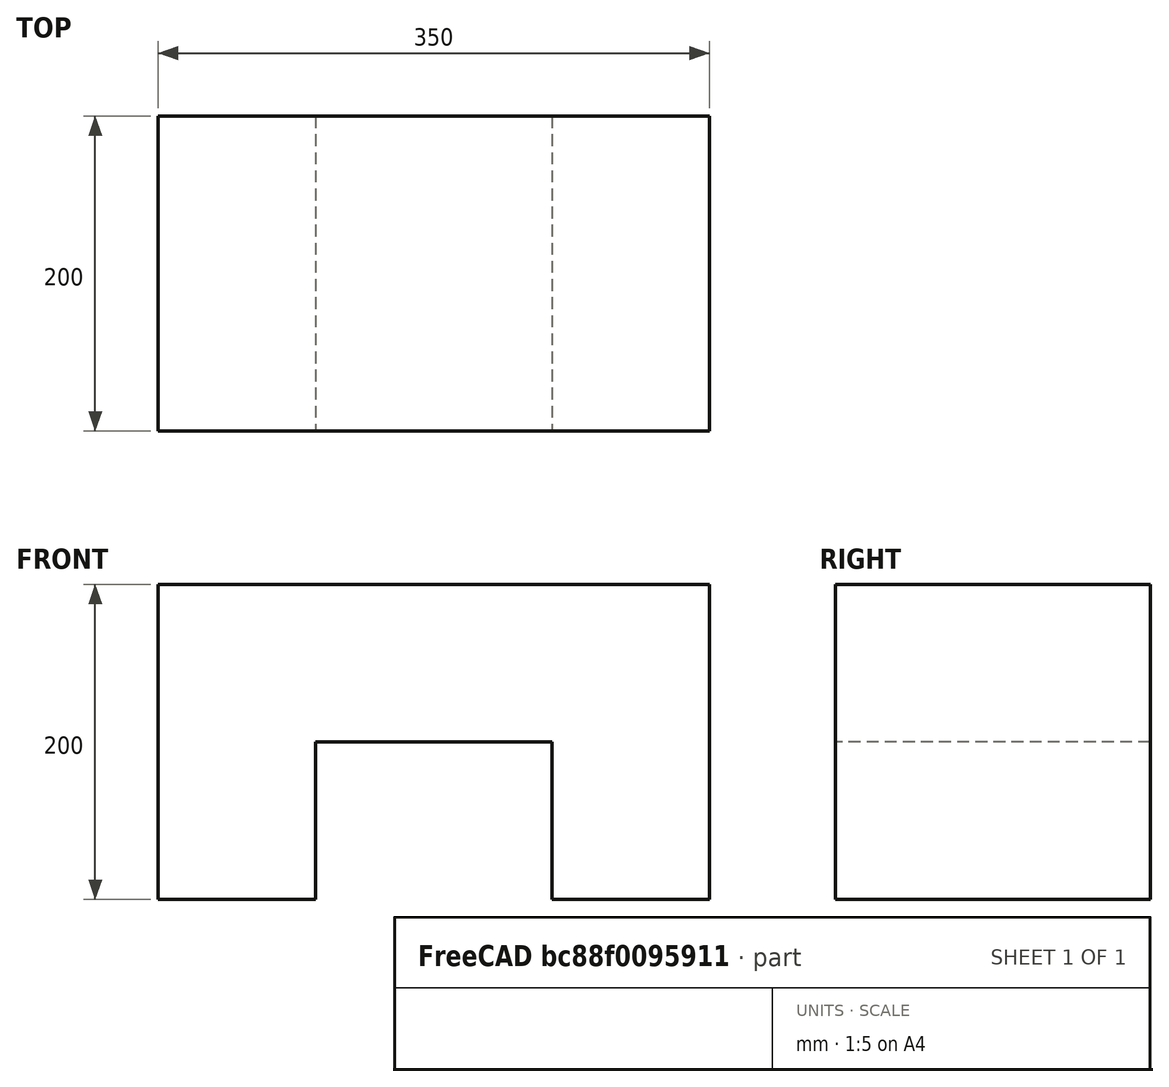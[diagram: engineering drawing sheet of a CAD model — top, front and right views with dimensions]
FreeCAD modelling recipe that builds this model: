
FCSTD DOCUMENT  (FreeCAD 0.16R6706 (Git))
Label: bridge
License: All rights reserved
LicenseURL: http://en.wikipedia.org/wiki/All_rights_reserved
objects: Sketcher::SketchObject×1, PartDesign::Pad×1, Drawing::FeatureViewPart×1, Drawing::FeaturePage×1
note: 3 computed .brp shape members not serialized (recipe doc carries the construction recipe); baked Part::Feature solids carry a one-line shape summary decoded from their .brp

FEATURE [Sketcher::SketchObject] Sketch
  Placement = pos=(0,0,0) rot=(-1,0,0;4.71239rad)
  sketch-geometry (8):
    g0: LineSegment StartX=-175 StartY=200 StartZ=0 EndX=-175 EndY=0 EndZ=0
    g1: LineSegment StartX=-175 StartY=0 StartZ=0 EndX=-75 EndY=0 EndZ=0
    g2: LineSegment StartX=-75 StartY=0 StartZ=0 EndX=-75 EndY=100 EndZ=0
    g3: LineSegment StartX=-75 StartY=100 StartZ=0 EndX=75 EndY=100 EndZ=0
    g4: LineSegment StartX=75 StartY=100 StartZ=0 EndX=75 EndY=0 EndZ=0
    g5: LineSegment StartX=75 StartY=0 StartZ=0 EndX=175 EndY=0 EndZ=0
    g6: LineSegment StartX=175 StartY=0 StartZ=0 EndX=175 EndY=200 EndZ=0
    g7: LineSegment StartX=175 StartY=200 StartZ=0 EndX=-175 EndY=200 EndZ=0
  constraints (24):
    c: Vertical(g0)
    c: Coincident(g0,g1)
    c: Horizontal(g1)
    c: Coincident(g1,g2)
    c: Vertical(g2)
    c: Coincident(g2,g3)
    c: Horizontal(g3)
    c: Coincident(g3,g4)
    c: Vertical(g4)
    c: Coincident(g4,g5)
    c: Horizontal(g5)
    c: Coincident(g5,g6)
    c: Vertical(g6)
    c: Coincident(g6,g7)
    c: Coincident(g7,g0)
    c: Horizontal(g7)
    c: PointOnObject(g1,g-1)
    c: PointOnObject(g4,g-1)
    c: Symmetric(g2,g3,g-2)
    c: DistanceX(g1,g1) = 100
    c: DistanceX(g1,g4) = 150
    c: Equal(g1,g5)
    c: DistanceY(g0,g0) = 200
    c: DistanceY(g2,g2) = 100
FEATURE [PartDesign::Pad] Pad
  Length = 200
  Length2 = 100
  Placement = pos=(0,0,0) rot=(-1,0,0;4.71239rad)
  Sketch = -> Sketch
  Type = 0
FEATURE [Drawing::FeatureViewPart] View
  Direction = (1,-1,1)
  HiddenWidth = 0.15
  LineWidth = 0.35
  Rotation = 60
  Scale = 0.2
  ShowHiddenLines = false
  ShowSmoothLines = false
  Source = -> Pad
  Tolerance = 0.05
  ViewResult = <g id="View"\n   transform="rotate(60,122.678,199.531) translate(122.678,199.531) scale(0.2,0.2)"\n  >\n<g   stroke="rgb(0, 0, 0)"\n   stroke-width="1.75"\n   stroke-linecap="butt"\n   stroke-linejoin="miter"\n   fill="none"\n   transform="scale(1,-1)"\n  >\n<path id= "1" d=" M -265.165 10.2062 L -265.165 -153.093 " />\n<path id= "2" d=" M -265.165 -153.093 L -123.744 -234.743 " />\n<path id= "3" d=" M -53.033 -112.268 L -53.033 -193.918 " />\n<path id= "4" d=" M -123.744 -234.743 L -53.033 -193.918 " />\n<path id= "5" d=" M -53.033 -193.918 L -123.744 -153.093 " />\n<path id= "6" d=" M -123.744 -153.093 L -17.6777 -91.8559 " />\n<path id= "7" d=" M -17.6777 -91.8559 L 53.033 -132.681 " />\n<path id= "8" d=" M 123.744 71.4435 L 123.744 -91.8559 " />\n<path id= "9" d=" M 53.033 -132.681 L 123.744 -91.8559 " />\n<path id= "10" d=" M -17.6777 153.093 L -17.6777 -10.2062 " />\n<path id= "11" d=" M 123.744 71.4435 L -17.6777 153.093 " />\n<path id= "12" d=" M 123.744 -91.8559 L -17.6777 -10.2062 " />\n<path id= "13" d=" M -17.6777 153.093 L -265.165 10.2062 " />\n<path id= "14" d=" M -17.6777 -10.2062 L -265.165 -153.093 " />\n</g>\n</g>
  Visible = true
  X = 122.678
  Y = 199.531
FEATURE [Drawing::FeaturePage] Page
  Group = -> [View]
